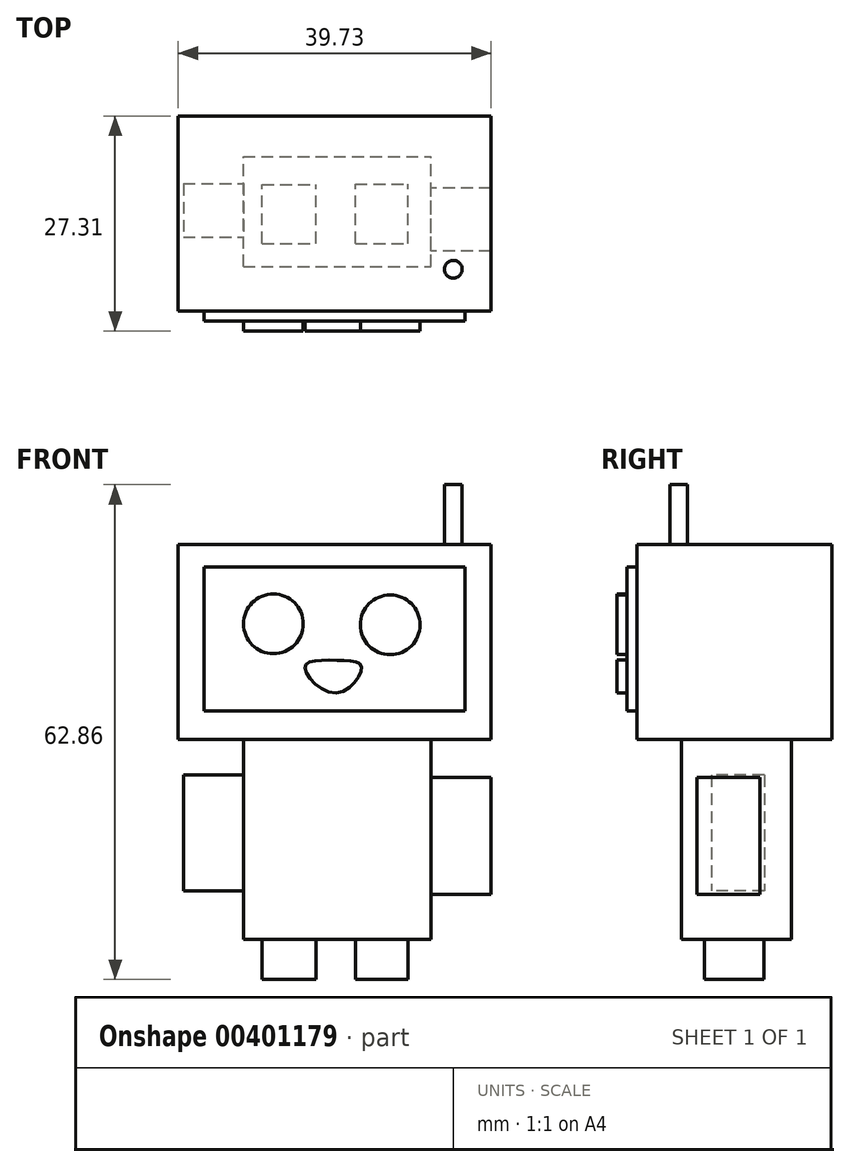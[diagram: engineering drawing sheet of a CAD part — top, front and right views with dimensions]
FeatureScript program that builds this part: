
annotation { "Feature Type Name" : "Feature", "Feature Type Description" : "" }
export const myFeature = defineFeature(function(context is Context, id is Id, definition is map)
    precondition{}
    {
        {
            var Q0;
            Q0=qCreatedBy(makeId("Front.planeOp"),FACE);
            var sketch = newSketch(context, id + "F0", { "sketchPlane" : qUnion([Q0])});
            skLineSegment(sketch, "E0.bottom", {"start": v(-20.04, 49.61) * mm, "end": v(19.67, 49.61) * mm});
            skLineSegment(sketch, "E0.top", {"start": v(-20.04, 24.85) * mm, "end": v(19.67, 24.85) * mm});
            skLineSegment(sketch, "E0.left", {"start": v(-20.04, 49.61) * mm, "end": v(-20.04, 24.85) * mm});
            skLineSegment(sketch, "E0.right", {"start": v(19.67, 49.61) * mm, "end": v(19.67, 24.85) * mm});
            skSolve(sketch);
        }
        {
            var Q0;
            Q0=makeQuery(id+"F0.imprint","IMPRINT",FACE,{"disambiguationData":[TD([[makeQuery(id+"F0.imprint","IMPRINT",EDGE,{"derivedFrom":sQuery(id+"F0.wireOp",EDGE,"E0.bottom")}),-1.0]])]});
            extrude(context, id + "F1", {"entities" : qUnion([Q0]), "depth" : 24.76 * mm});
        }
        {
            var Q0;
            Q0=makeQuery(id+"F1.opExtrude","SWEPT_FACE",FACE,{"disambiguationData":[OSD([sQuery(id+"F0.wireOp",EDGE,"E0.top")])]});
            var sketch = newSketch(context, id + "F2", { "sketchPlane" : qUnion([Q0])});
            skLineSegment(sketch, "E1.bottom", {"start": v(-11.77, 19.12) * mm, "end": v(12.07, 19.12) * mm});
            skLineSegment(sketch, "E1.top", {"start": v(-11.77, 5.12) * mm, "end": v(12.07, 5.12) * mm});
            skLineSegment(sketch, "E1.left", {"start": v(-11.77, 19.12) * mm, "end": v(-11.77, 5.12) * mm});
            skLineSegment(sketch, "E1.right", {"start": v(12.07, 19.12) * mm, "end": v(12.07, 5.12) * mm});
            skSolve(sketch);
        }
        {
            var Q0;
            Q0=makeQuery(id+"F2.imprint","IMPRINT",FACE,{"disambiguationData":[TD([[makeQuery(id+"F2.imprint","IMPRINT",EDGE,{"derivedFrom":sQuery(id+"F2.wireOp",EDGE,"E1.bottom")}),-1.0]])]});
            extrude(context, id + "F3", {"entities" : qUnion([Q0]), "operationType" : NewBodyOperationType.ADD, "depth" : 25.4 * mm});
        }
        {
            var Q0;
            Q0=makeQuery(id+"F3.opExtrude","SWEPT_FACE",FACE,{"disambiguationData":[OSD([sQuery(id+"F2.wireOp",EDGE,"E1.left")])]});
            var sketch = newSketch(context, id + "F4", { "sketchPlane" : qUnion([Q0])});
            skLineSegment(sketch, "E2.bottom", {"start": v(8.6, 20.32) * mm, "end": v(15.34, 20.32) * mm});
            skLineSegment(sketch, "E2.top", {"start": v(8.6, 5.62) * mm, "end": v(15.34, 5.62) * mm});
            skLineSegment(sketch, "E2.left", {"start": v(8.6, 20.32) * mm, "end": v(8.6, 5.62) * mm});
            skLineSegment(sketch, "E2.right", {"start": v(15.34, 20.32) * mm, "end": v(15.34, 5.62) * mm});
            skSolve(sketch);
        }
        {
            var Q0;
            Q0=makeQuery(id+"F4.imprint","IMPRINT",FACE,{"disambiguationData":[TD([[makeQuery(id+"F4.imprint","IMPRINT",EDGE,{"derivedFrom":sQuery(id+"F4.wireOp",EDGE,"E2.bottom")}),-1.0]])]});
            extrude(context, id + "F5", {"entities" : qUnion([Q0]), "operationType" : NewBodyOperationType.ADD, "depth" : 7.62 * mm});
        }
        {
            var Q0;
            Q0=makeQuery(id+"F3.opExtrude","SWEPT_FACE",FACE,{"disambiguationData":[OSD([sQuery(id+"F2.wireOp",EDGE,"E1.right")])]});
            var sketch = newSketch(context, id + "F6", { "sketchPlane" : qUnion([Q0])});
            skLineSegment(sketch, "E3.bottom", {"start": v(-17.13, 20.02) * mm, "end": v(-9.13, 20.02) * mm});
            skLineSegment(sketch, "E3.top", {"start": v(-17.13, 5.16) * mm, "end": v(-9.13, 5.16) * mm});
            skLineSegment(sketch, "E3.left", {"start": v(-17.13, 20.02) * mm, "end": v(-17.13, 5.16) * mm});
            skLineSegment(sketch, "E3.right", {"start": v(-9.13, 20.02) * mm, "end": v(-9.13, 5.16) * mm});
            skSolve(sketch);
        }
        {
            var Q0;
            Q0=makeQuery(id+"F6.imprint","IMPRINT",FACE,{"disambiguationData":[TD([[makeQuery(id+"F6.imprint","IMPRINT",EDGE,{"derivedFrom":sQuery(id+"F6.wireOp",EDGE,"E3.bottom")}),-1.0]])]});
            extrude(context, id + "F7", {"entities" : qUnion([Q0]), "operationType" : NewBodyOperationType.ADD, "depth" : 7.62 * mm});
        }
        {
            var Q0;
            Q0=makeQuery(id+"F3.opExtrude","CAP_FACE",FACE,{"disambiguationData":[OSD([sQuery(id+"F2.wireOp",EDGE,"E1.bottom"),sQuery(id+"F2.wireOp",EDGE,"E1.top"),sQuery(id+"F2.wireOp",EDGE,"E1.left"),sQuery(id+"F2.wireOp",EDGE,"E1.right")])],"isStart":false});
            var sketch = newSketch(context, id + "F8", { "sketchPlane" : qUnion([Q0])});
            skLineSegment(sketch, "E4.bottom", {"start": v(-9.4, 16.17) * mm, "end": v(-2.55, 16.17) * mm});
            skLineSegment(sketch, "E4.top", {"start": v(-9.4, 8.72) * mm, "end": v(-2.55, 8.72) * mm});
            skLineSegment(sketch, "E4.left", {"start": v(-9.4, 16.17) * mm, "end": v(-9.4, 8.72) * mm});
            skLineSegment(sketch, "E4.right", {"start": v(-2.55, 16.17) * mm, "end": v(-2.55, 8.72) * mm});
            skPoint(sketch, "E5.firstSnap0", {"position": v(-5.97, 16.17) * mm});
            skLineSegment(sketch, "E5.bottom", {"start": v(2.46, 16.17) * mm, "end": v(9.16, 16.17) * mm});
            skLineSegment(sketch, "E5.top", {"start": v(2.46, 8.64) * mm, "end": v(9.16, 8.64) * mm});
            skLineSegment(sketch, "E5.left", {"start": v(2.46, 16.17) * mm, "end": v(2.46, 8.64) * mm});
            skLineSegment(sketch, "E5.right", {"start": v(9.16, 16.17) * mm, "end": v(9.16, 8.64) * mm});
            skSolve(sketch);
        }
        {
            var Q0;
            Q0=makeQuery(id+"F8.imprint","IMPRINT",FACE,{"disambiguationData":[TD([[makeQuery(id+"F8.imprint","IMPRINT",EDGE,{"derivedFrom":sQuery(id+"F8.wireOp",EDGE,"E4.bottom")}),-1.0]])]});
            var Q1;
            Q1=makeQuery(id+"F8.imprint","IMPRINT",FACE,{"disambiguationData":[TD([[makeQuery(id+"F8.imprint","IMPRINT",EDGE,{"derivedFrom":sQuery(id+"F8.wireOp",EDGE,"E5.bottom")}),-1.0]])]});
            extrude(context, id + "F9", {"entities" : qUnion([Q0, Q1]), "operationType" : NewBodyOperationType.ADD, "depth" : 5.08 * mm});
        }
        {
            var Q0;
            Q0=makeQuery(id+"F1.opExtrude","CAP_FACE",FACE,{"disambiguationData":[OSD([sQuery(id+"F0.wireOp",EDGE,"E0.bottom"),sQuery(id+"F0.wireOp",EDGE,"E0.top"),sQuery(id+"F0.wireOp",EDGE,"E0.left"),sQuery(id+"F0.wireOp",EDGE,"E0.right")])],"isStart":false});
            var sketch = newSketch(context, id + "F10", { "sketchPlane" : qUnion([Q0])});
            skLineSegment(sketch, "E6.bottom", {"start": v(-16.79, 46.73) * mm, "end": v(16.36, 46.73) * mm});
            skLineSegment(sketch, "E6.top", {"start": v(-16.79, 28.5) * mm, "end": v(16.36, 28.5) * mm});
            skLineSegment(sketch, "E6.left", {"start": v(-16.79, 46.73) * mm, "end": v(-16.79, 28.5) * mm});
            skLineSegment(sketch, "E6.right", {"start": v(16.36, 46.73) * mm, "end": v(16.36, 28.5) * mm});
            skSolve(sketch);
        }
        {
            var Q0;
            Q0=makeQuery(id+"F10.imprint","IMPRINT",FACE,{"disambiguationData":[TD([[makeQuery(id+"F10.imprint","IMPRINT",EDGE,{"derivedFrom":sQuery(id+"F10.wireOp",EDGE,"E6.bottom")}),-1.0]])]});
            extrude(context, id + "F11", {"entities" : qUnion([Q0]), "operationType" : NewBodyOperationType.ADD, "depth" : 1.27 * mm});
        }
        {
            var Q0;
            Q0=makeQuery(id+"F11.opExtrude","CAP_FACE",FACE,{"disambiguationData":[OSD([sQuery(id+"F10.wireOp",EDGE,"E6.bottom"),sQuery(id+"F10.wireOp",EDGE,"E6.top"),sQuery(id+"F10.wireOp",EDGE,"E6.left"),sQuery(id+"F10.wireOp",EDGE,"E6.right")])],"isStart":false});
            var sketch = newSketch(context, id + "F12", { "sketchPlane" : qUnion([Q0])});
            skCircle(sketch, "E7", {"center": v(6.9, 39.42) * mm, "radius": 3.8 * mm});
            skCircle(sketch, "E8", {"center": v(-7.96, 39.54) * mm, "radius": 3.8 * mm});
            skFitSpline(sketch, "E9", {"points": [v(3.24, 34.07) * mm, v(0, 34.92) * mm, v(-3.94, 34.07) * mm, v(0, 30.78) * mm, v(3.24, 34.07) * mm]});
            skSolve(sketch);
        }
        {
            var Q0;
            Q0=makeQuery(id+"F12.imprint","IMPRINT",FACE,{"disambiguationData":[TD([[makeQuery(id+"F12.imprint","IMPRINT",EDGE,{"derivedFrom":sQuery(id+"F12.wireOp",EDGE,"E8")}),1.0]])]});
            var Q1;
            Q1=makeQuery(id+"F12.imprint","IMPRINT",FACE,{"disambiguationData":[TD([[makeQuery(id+"F12.imprint","IMPRINT",EDGE,{"derivedFrom":sQuery(id+"F12.wireOp",EDGE,"E7")}),1.0]])]});
            var Q2;
            Q2=makeQuery(id+"F12.imprint","IMPRINT",FACE,{"disambiguationData":[TD([[makeQuery(id+"F12.imprint","IMPRINT",EDGE,{"derivedFrom":sQuery(id+"F12.wireOp",EDGE,"E9")}),1.0]])]});
            extrude(context, id + "F13", {"entities" : qUnion([Q0, Q1, Q2]), "operationType" : NewBodyOperationType.ADD, "depth" : 1.27 * mm});
        }
        {
            var Q0;
            Q0=makeQuery(id+"F1.opExtrude","SWEPT_FACE",FACE,{"disambiguationData":[OSD([sQuery(id+"F0.wireOp",EDGE,"E0.bottom")])]});
            var sketch = newSketch(context, id + "F14", { "sketchPlane" : qUnion([Q0])});
            skCircle(sketch, "E10", {"center": v(14.9, -19.46) * mm, "radius": 1.13 * mm});
            skSolve(sketch);
        }
        {
            var Q0;
            Q0=makeQuery(id+"F14.imprint","IMPRINT",FACE,{"disambiguationData":[TD([[makeQuery(id+"F14.imprint","IMPRINT",EDGE,{"derivedFrom":sQuery(id+"F14.wireOp",EDGE,"E10")}),1.0]])]});
            extrude(context, id + "F15", {"entities" : qUnion([Q0]), "operationType" : NewBodyOperationType.ADD, "depth" : 7.62 * mm});
        }
    });
